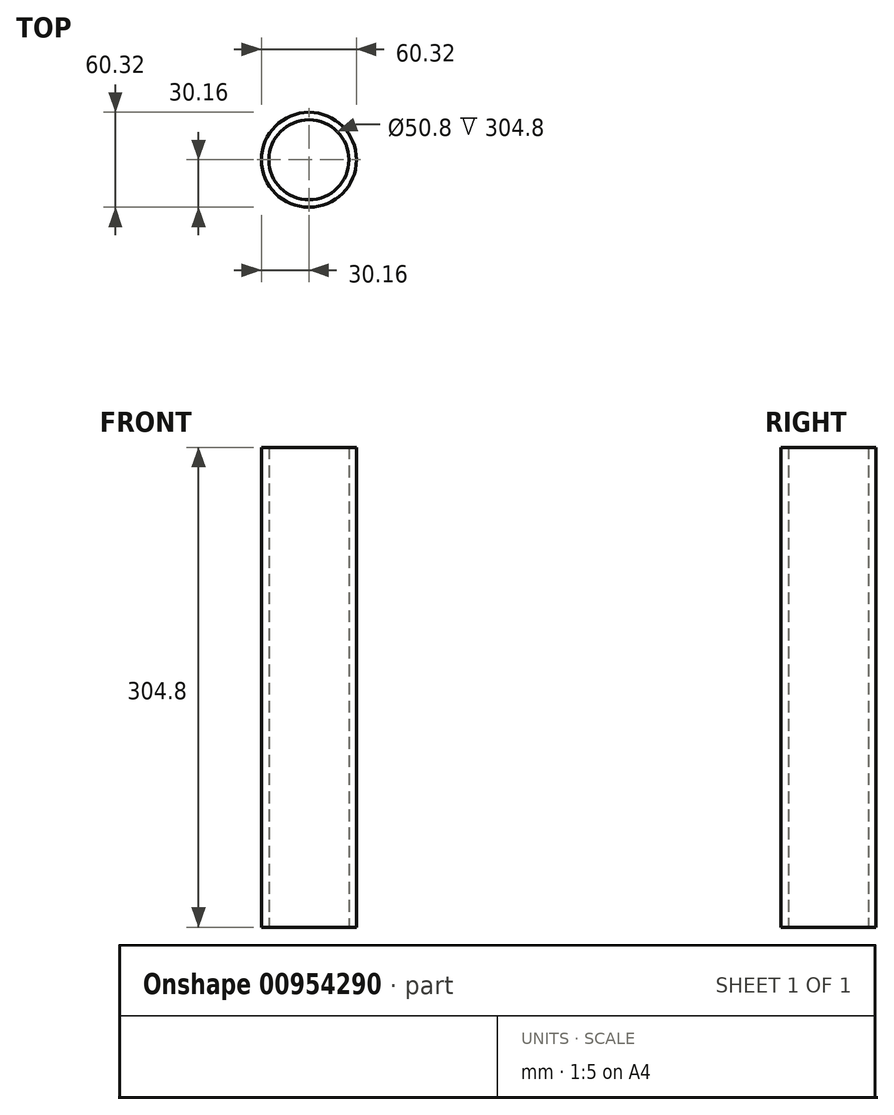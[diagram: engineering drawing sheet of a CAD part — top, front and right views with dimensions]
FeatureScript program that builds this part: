
annotation { "Feature Type Name" : "Feature", "Feature Type Description" : "" }
export const myFeature = defineFeature(function(context is Context, id is Id, definition is map)
    precondition{}
    {
        {
            var Q0;
            Q0=qCreatedBy(makeId("Top.planeOp"),FACE);
            var sketch = newSketch(context, id + "F0", { "sketchPlane" : qUnion([Q0])});
            skCircle(sketch, "E0", {"center": v(0, 0) * mm, "radius": 25.4 * mm});
            skCircle(sketch, "E1", {"center": v(0, 0) * mm, "radius": 30.16 * mm});
            skSolve(sketch);
        }
        {
            var Q0;
            Q0=makeQuery(id+"F0.imprint","IMPRINT",FACE,{"disambiguationData":[TD([[makeQuery(id+"F0.imprint","IMPRINT",EDGE,{"derivedFrom":sQuery(id+"F0.wireOp",EDGE,"E0")}),-1.0]])]});
            extrude(context, id + "F1", {"entities" : qUnion([Q0]), "offsetDistance" : 25.4 * mm, "depth" : 152.4 * mm, "hasSecondDirection" : true, "secondDirectionOppositeDirection" : true, "secondDirectionDepth" : 152.4 * mm});
        }
    });
